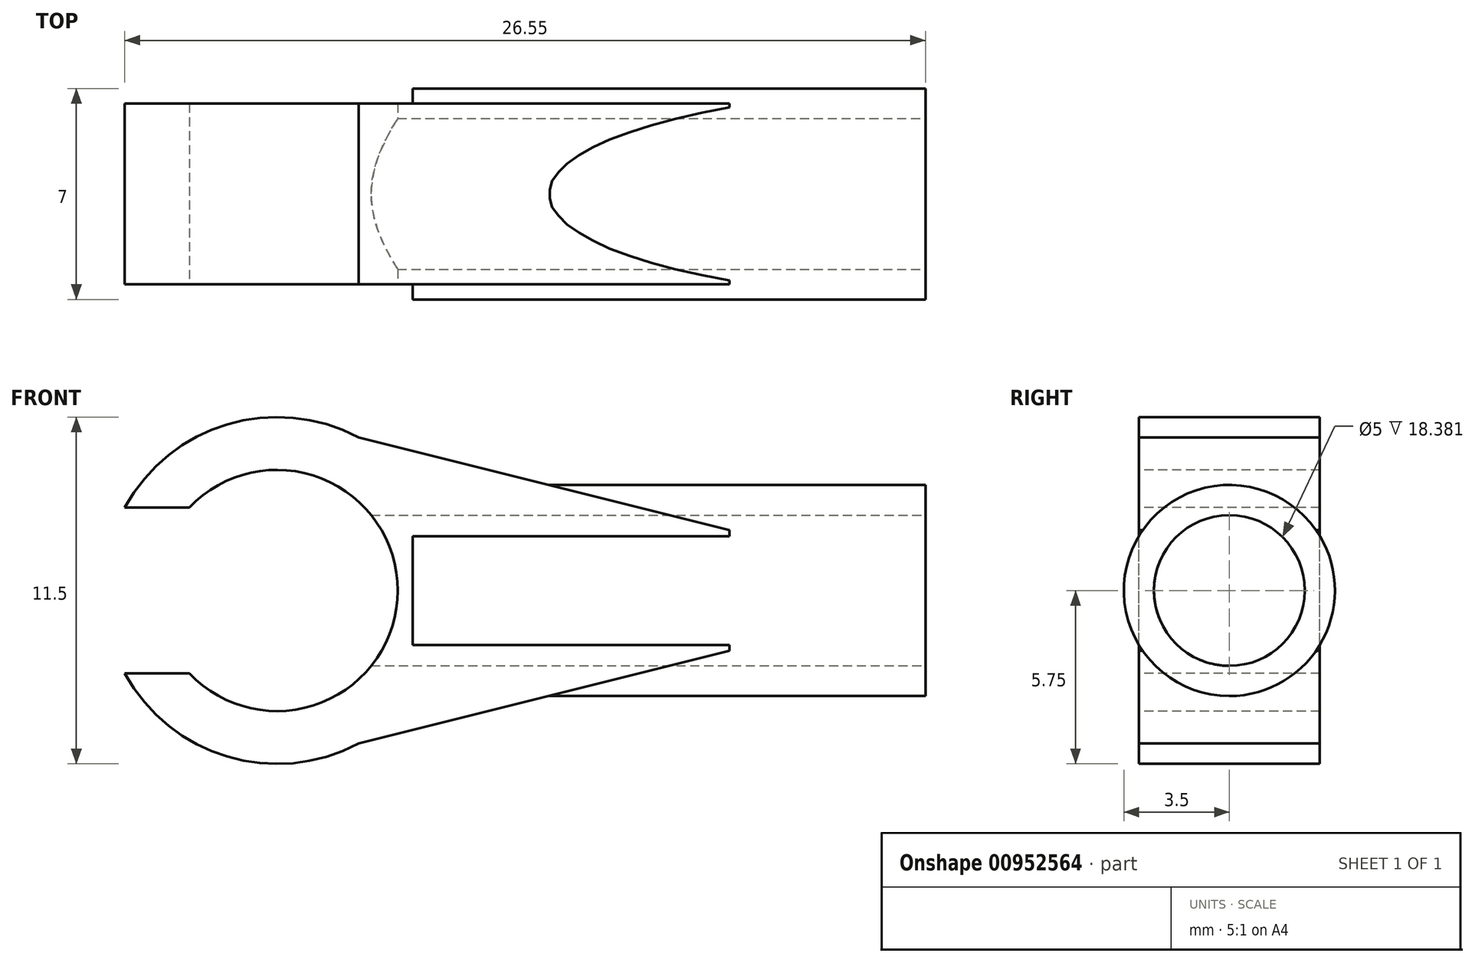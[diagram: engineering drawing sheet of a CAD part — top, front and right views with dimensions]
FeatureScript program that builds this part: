
annotation { "Feature Type Name" : "Feature", "Feature Type Description" : "" }
export const myFeature = defineFeature(function(context is Context, id is Id, definition is map)
    precondition{}
    {
        {
            var Q0;
            Q0=qCreatedBy(makeId("Front.planeOp"),FACE);
            var sketch = newSketch(context, id + "F0", { "sketchPlane" : qUnion([Q0])});
            skCircle(sketch, "E0", {"center": v(0, 0) * mm, "radius": 4 * mm});
            skCircle(sketch, "E1", {"center": v(0, 0) * mm, "radius": 5.75 * mm});
            skSolve(sketch);
        }
        {
            var Q0;
            Q0 = qSketchRegion(id + "F0", true);
            extrude(context, id + "F1", {"entities" : qUnion([Q0]), "endBound" : BoundingType.SYMMETRIC, "oppositeDirection" : true, "depth" : 6 * mm, "offsetDistance" : 25 * mm});
        }
        {
            var Q0;
            Q0=qCreatedBy(makeId("Right.planeOp"),FACE);
            cPlane(context, id + "F2", {"entities" : qUnion([Q0]), "cplaneType" : CPlaneType.OFFSET, "offset" : 4.5 * mm, "width" : 150 * mm, "height" : 150 * mm});
        }
        {
            var Q0;
            Q0=qCreatedBy(id+"F2.planeOp",FACE);
            var sketch = newSketch(context, id + "F3", { "sketchPlane" : qUnion([Q0])});
            skCircle(sketch, "E2", {"center": v(0, 0) * mm, "radius": 3.5 * mm});
            skSolve(sketch);
        }
        {
            var Q0;
            Q0 = qSketchRegion(id + "F3", true);
            extrude(context, id + "F4", {"entities" : qUnion([Q0]), "operationType" : NewBodyOperationType.ADD, "depth" : 17 * mm, "offsetDistance" : 25 * mm});
        }
        {
            var Q0;
            Q0=makeQuery(id+"F1.opExtrude","CAP_FACE",FACE,{"disambiguationData":[OSD([sQuery(id+"F0.wireOp",EDGE,"E0"),sQuery(id+"F0.wireOp",EDGE,"E1")])],"isStart":true});
            var sketch = newSketch(context, id + "F5", { "sketchPlane" : qUnion([Q0])});
            skLineSegment(sketch, "E3.bottom", {"start": v(-20, 2.75) * mm, "end": v(0, 2.75) * mm});
            skLineSegment(sketch, "E3.top", {"start": v(-20, -2.75) * mm, "end": v(0, -2.75) * mm});
            skLineSegment(sketch, "E3.left", {"start": v(-20, 2.75) * mm, "end": v(-20, -2.75) * mm});
            skLineSegment(sketch, "E3.right", {"start": v(0, 2.75) * mm, "end": v(0, -2.75) * mm});
            skPoint(sketch, "E4", {"position": v(-20, 0) * mm});
            skSolve(sketch);
        }
        {
            var Q0;
            Q0 = qSketchRegion(id + "F5", true);
            extrude(context, id + "F6", {"entities" : qUnion([Q0]), "operationType" : NewBodyOperationType.REMOVE, "oppositeDirection" : true, "depth" : 25 * mm, "offsetDistance" : 25 * mm});
        }
        {
            var Q0;
            Q0=qCreatedBy(id+"F2.planeOp",FACE);
            cPlane(context, id + "F7", {"entities" : qUnion([Q0]), "cplaneType" : CPlaneType.OFFSET, "offset" : 12 * mm, "width" : 150 * mm, "height" : 150 * mm});
        }
        {
            var Q0;
            Q0=qCreatedBy(id+"F7.planeOp",FACE);
            var sketch = newSketch(context, id + "F8", { "sketchPlane" : qUnion([Q0])});
            skLineSegment(sketch, "E5", {"start": v(-2.5, 0) * mm, "end": v(2.5, 0) * mm, "construction": true});
            skPoint(sketch, "E6", {"position": v(0, 0) * mm});
            skArc(sketch, "E7", {"start": v(3.5, 0) * mm, "mid": v(2.5, 1) * mm, "end": v(1.5, 0) * mm});
            skLineSegment(sketch, "E8", {"start": v(0, 0) * mm, "end": v(0, -1.96) * mm, "construction": true});
            skArc(sketch, "E9.MirrorCS", {"start": v(-3.5, 0) * mm, "mid": v(-2.5, 1) * mm, "end": v(-1.5, 0) * mm});
            skSolve(sketch);
        }
        {
            var Q0;
            Q0=qCreatedBy(id+"F7.planeOp",FACE);
            var sketch = newSketch(context, id + "F9", { "sketchPlane" : qUnion([Q0])});
            skLineSegment(sketch, "E10", {"start": v(-4.04, 0) * mm, "end": v(4.97, 0) * mm, "construction": true});
            skSolve(sketch);
        }
        {
            var Q0;
            Q0=makeQuery(id+"F4.opExtrude","CAP_FACE",FACE,{"disambiguationData":[OSD([sQuery(id+"F3.wireOp",EDGE,"E2")])],"isStart":false});
            var sketch = newSketch(context, id + "F10", { "sketchPlane" : qUnion([Q0])});
            skCircle(sketch, "E11", {"center": v(0, 0) * mm, "radius": 2.5 * mm});
            skSolve(sketch);
        }
        {
            var Q0;
            {var subQ0=sQuery(id+"F3.wireOp",EDGE,"E2");var subQ1=sQuery(id+"F0.wireOp",EDGE,"E1");var subQ2=sQuery(id+"F0.wireOp",EDGE,"E0");var subQ3=makeQuery(id+"F1.opExtrude","CAP_FACE",FACE,{"disambiguationData":[OSD([subQ2,subQ1])],"isStart":true});Q0=makeQuery(id+"F5.imprint","IMPRINT",FACE,{"disambiguationData":[TD([[makeQuery(id+"F5.imprint","IMPRINT",EDGE,{"derivedFrom":makeQuery(id+"F4.boolean.opBoolean","INTERSECT",EDGE,{"derivedFrom":[subQ3,makeQuery(id+"F4.opExtrude","CAP_FACE",FACE,{"disambiguationData":[OSD([subQ0])],"isStart":true})]})}),1.0]])]});}
            var sketch = newSketch(context, id + "F11", { "sketchPlane" : qUnion([Q0])});
            skLineSegment(sketch, "E12", {"start": v(0, 5.75) * mm, "end": v(15, 2) * mm});
            skLineSegment(sketch, "E13", {"start": v(15, 2) * mm, "end": v(15, -2) * mm});
            skLineSegment(sketch, "E14", {"start": v(15, -2) * mm, "end": v(0, -5.75) * mm});
            skLineSegment(sketch, "E15", {"start": v(0, 7.1) * mm, "end": v(0, -6.9) * mm, "construction": true});
            skPoint(sketch, "E16", {"position": v(15, 0) * mm});
            skLineSegment(sketch, "E17", {"start": v(0, 5.75) * mm, "end": v(4.89, 1.13) * mm});
            skLineSegment(sketch, "E18", {"start": v(4.89, -0.96) * mm, "end": v(0, -5.75) * mm});
            skLineSegment(sketch, "E19", {"start": v(4.89, 1.13) * mm, "end": v(4.89, -0.96) * mm});
            skSolve(sketch);
        }
        {
            var Q0;
            Q0 = qSketchRegion(id + "F11", true);
            extrude(context, id + "F12", {"entities" : qUnion([Q0]), "operationType" : NewBodyOperationType.ADD, "oppositeDirection" : true, "depth" : 6 * mm, "offsetDistance" : 25 * mm});
        }
        {
            var Q0;
            Q0 = qSketchRegion(id + "F10", true);
            extrude(context, id + "F13", {"entities" : qUnion([Q0]), "operationType" : NewBodyOperationType.REMOVE, "oppositeDirection" : true, "depth" : 25 * mm, "offsetDistance" : 25 * mm});
        }
    });
